# Revit family: NRG4000
name_source: partatom
category: Lighting Fixtures
revit_build: Autodesk Revit Architecture 2012 (Build: 20110309_2315(x64)
units: mm (PartAtom-declared; Revit-internal decimal feet)

## types (1)
- NRG 4000
    Color Filter = 16777215
    Default Elevation = 48"
    Description = Ceiling mount applications including parking garages, walkways, building eaves, drive under canopies, etc.
    Dimming Lamp Color Temperature Shift = <None>
    Emit Shape Visible in Rendering = No
    Emit from Circle Diameter = 5"
    Finish = Bronze
    Finish2 = Bronze
    Lamp = One
    Light Source Symbol Size = 5"
    Manufacturer = Hubbell Outdoor Lighting
    Manufacturer Fax = (864)-678-1065
    Model = NRG 4000
    Opal lens = Etched Glass
    Product Documentation Link = http://www.hubbelloutdoor.com
    Product Page URL = http://www.hubbelloutdoor.com
    URL = http://www.hubbelloutdoor.com
    Wattage Comments = 100W/120W

## geometry (parser evidence)
native form markers: Sweep x2
no freeform markers — native parametric forms only
